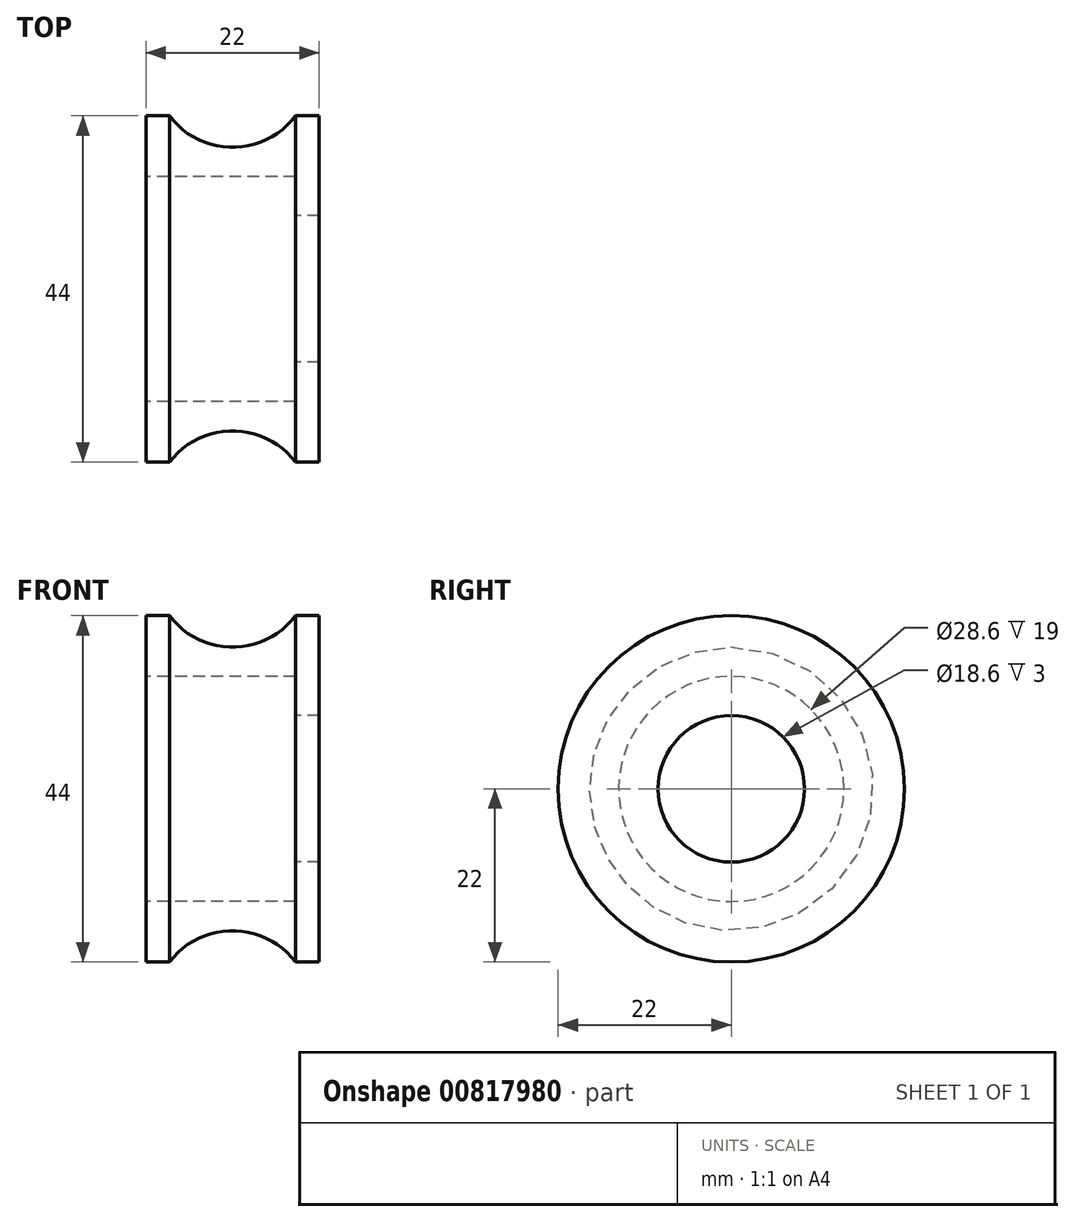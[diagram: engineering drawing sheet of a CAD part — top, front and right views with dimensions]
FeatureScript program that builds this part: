
annotation { "Feature Type Name" : "Feature", "Feature Type Description" : "" }
export const myFeature = defineFeature(function(context is Context, id is Id, definition is map)
    precondition{}
    {
        {
            var Q0;
            Q0=qCreatedBy(makeId("Front.planeOp"),FACE);
            var sketch = newSketch(context, id + "F0", { "sketchPlane" : qUnion([Q0])});
            skLineSegment(sketch, "E0", {"start": v(-6.28, 14.3) * mm, "end": v(12.72, 14.3) * mm});
            skLineSegment(sketch, "E1", {"start": v(12.72, 14.3) * mm, "end": v(12.72, 9.3) * mm});
            skLineSegment(sketch, "E2", {"start": v(12.72, 9.3) * mm, "end": v(15.72, 9.3) * mm});
            skLineSegment(sketch, "E3", {"start": v(15.72, 9.3) * mm, "end": v(15.72, 22) * mm});
            skLineSegment(sketch, "E4", {"start": v(-6.28, 14.3) * mm, "end": v(-6.28, 22) * mm});
            skLineSegment(sketch, "E5", {"start": v(-6.28, 22) * mm, "end": v(-3.28, 22) * mm});
            skLineSegment(sketch, "E6", {"start": v(15.72, 22) * mm, "end": v(12.72, 22) * mm});
            skArc(sketch, "E7", {"start": v(-3.28, 22) * mm, "mid": v(4.72, 18) * mm, "end": v(12.72, 22) * mm});
            skLineSegment(sketch, "E8", {"start": v(-23, 0) * mm, "end": v(21.78, 0) * mm});
            skSolve(sketch);
        }
        {
            var Q0;
            Q0 = qSketchRegion(id + "F0", true);
            var Q1;
            Q1=sQuery(id+"F0.wireOp",EDGE,"E8");
            revolve(context, id + "F1", {"surfaceOperationType" : NewSurfaceOperationType.NEW, "entities" : qUnion([Q0]), "axis" : qUnion([Q1]), "revolveType" : RevolveType.FULL});
        }
    });
